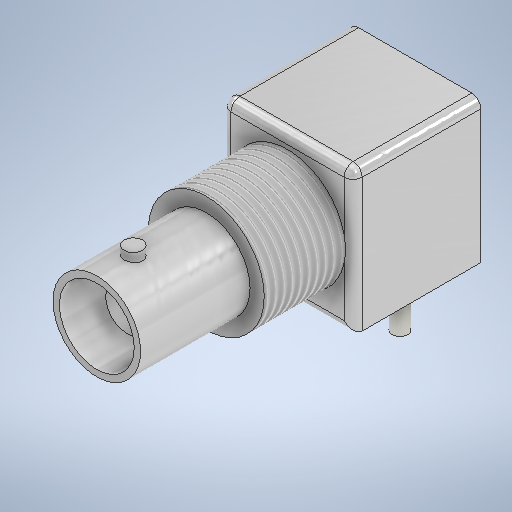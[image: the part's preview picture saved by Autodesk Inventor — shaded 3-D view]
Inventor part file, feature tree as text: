
AUTODESK INVENTOR PART (.ipt)
format: ipt  version: 2025 (Build 290162000, 162)  size: 423,936 bytes
history: native  units: in
note: dims shown in document units (in); Inventor stores cm internally (conversion verified against a paired STEP export)
features: sketch x9, extrude x6, plane x2, thread x1, fillet x1, revolve x1, sweep x1
ambient origin geometry x8: Origin, YZ Plane, XZ Plane, XY Plane, X Axis, Y Axis, Z Axis, Center Point
bodies: Body1 (feature_tree), Body2 (feature_tree)
feature tree (21):
  extrude  "Extrusion3"  Depth=0.5669in
  extrude  "Extrusion4"  Depth=0.5in
  thread  "Thread1"  [1 undecoded]
  fillet  "Fillet1"  Radius=0.3504in
  extrude  "Extrusion5"  Depth=0.378in
  plane  "Work Plane2"
  revolve  "Revolution1"  [1 undecoded]
  extrude  "Extrusion6"  Depth=0.0354in
  extrude  "Extrusion7"  TaperAngle=90.0deg  [1 undecoded]
  extrude  "Extrusion8"  Depth=0.3417in TaperAngle=0.0deg
  sketch  "Sketch12"  dims[d28=0.0681in d29=0.2854in]
  plane  "Work Plane3"
  sweep  "Sweep2"
  sketch  "Sketch5"  dims[d7=0.5669in d8=0.6142in]
  sketch  "Sketch6"  dims[d9=0.5512in d10=0.0in d11=0.5in d12=0.3504in d13=0.0in d14=0.3504in d15=0.0in]
  sketch  "Sketch7"  dims[d16=0.0394in d17=0.378in]
  sketch  "Sketch8"  dims[d18=0.4724in d19=0.0in d20=0.3228in]
  sketch  "Sketch9"  dims[d21=-0.1575in d22=0.0354in]
  sketch  "Sketch10"  dims[d23=0.0394in d24=90.0deg]
  sketch  "Sketch11"  dims[d25=0.185in d26=0.3417in d27=0.0in]
  sketch  "Sketch14"  dims[d30=0.2in d31=0.1614in d32=0.0in d33=0.0551in d34=0.0551in d35=0.0551in d36=0.1339in d37=0.1299in d38=0.1693in d39=0.1693in d40=0.2598in d41=0.2598in d42=0.2559in d43=0.1555in d44=0.1772in d45=0.1772in d46=0.1772in d47=0.0in d48=0.3169in d49=0.0299in d50=0.0283in d51=0.1in d53=0.4854in d54=0.3169in d55=0.0591in d56=0.0in d57=0.0in d4=0.0in d5=0.0in d6=0.0in]
note: 3 required parameter values undecoded (feature->parameter linkage not recoverable at this tier; creation-order binding heuristic only, values carry confidence <= 0.55)